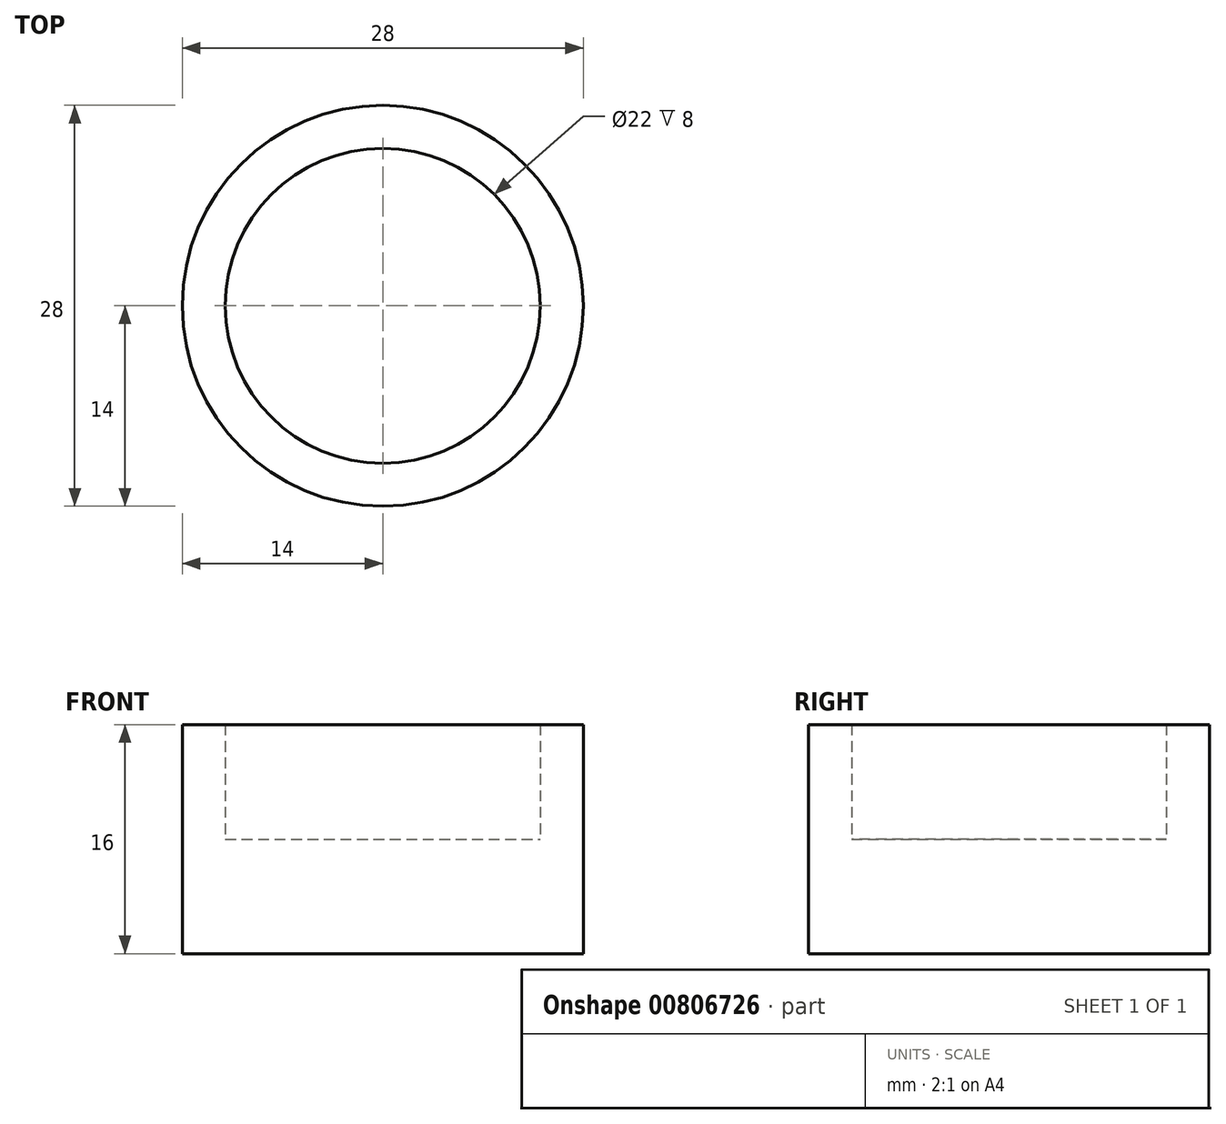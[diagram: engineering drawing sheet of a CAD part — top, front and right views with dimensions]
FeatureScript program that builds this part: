
annotation { "Feature Type Name" : "Feature", "Feature Type Description" : "" }
export const myFeature = defineFeature(function(context is Context, id is Id, definition is map)
    precondition{}
    {
        {
            var Q0;
            Q0=qCreatedBy(makeId("Front.planeOp"),FACE);
            var sketch = newSketch(context, id + "F0", { "sketchPlane" : qUnion([Q0])});
            skLineSegment(sketch, "E0", {"start": v(0, 0) * mm, "end": v(0, 85.08) * mm, "construction": true});
            skLineSegment(sketch, "E1", {"start": v(0, 0) * mm, "end": v(14, 0) * mm});
            skLineSegment(sketch, "E2", {"start": v(14, 0) * mm, "end": v(14, 16) * mm});
            skLineSegment(sketch, "E3", {"start": v(14, 16) * mm, "end": v(11, 16) * mm});
            skLineSegment(sketch, "E4", {"start": v(11, 16) * mm, "end": v(11, 8) * mm});
            skLineSegment(sketch, "E5", {"start": v(11, 8) * mm, "end": v(0, 8) * mm});
            skLineSegment(sketch, "E6", {"start": v(0, 8) * mm, "end": v(0, 0) * mm});
            skSolve(sketch);
        }
        {
            var Q0;
            Q0=makeQuery(id+"F0.imprint","IMPRINT",FACE,{"disambiguationData":[TD([[makeQuery(id+"F0.imprint","IMPRINT",EDGE,{"derivedFrom":sQuery(id+"F0.wireOp",EDGE,"E1")}),1.0]])]});
            var Q1;
            Q1=sQuery(id+"F0.wireOp",EDGE,"E0");
            revolve(context, id + "F1", {"surfaceOperationType" : NewSurfaceOperationType.NEW, "entities" : qUnion([Q0]), "axis" : qUnion([Q1]), "revolveType" : RevolveType.FULL});
        }
    });
